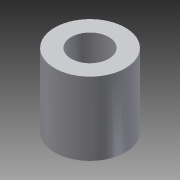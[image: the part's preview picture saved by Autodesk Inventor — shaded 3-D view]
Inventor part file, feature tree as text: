
AUTODESK INVENTOR PART (.ipt)
format: ipt  version: 2013 (Build 170138000, 138)  size: 77,824 bytes
history: native  units: in
note: dims shown in document units (in); Inventor stores cm internally (conversion verified against a paired STEP export)
features: extrude x1, sketch x1
ambient origin geometry x8: Origin, YZ Plane, XZ Plane, XY Plane, X Axis, Y Axis, Z Axis, Center Point
bodies: Solid1 (feature_tree)
feature tree (2):
  extrude  "Extrusion1"  Depth=0.2in
  sketch  "Sketch1"  dims[d0=0.375in d1=0.2in d2=0.3875in d3=0.0in]
